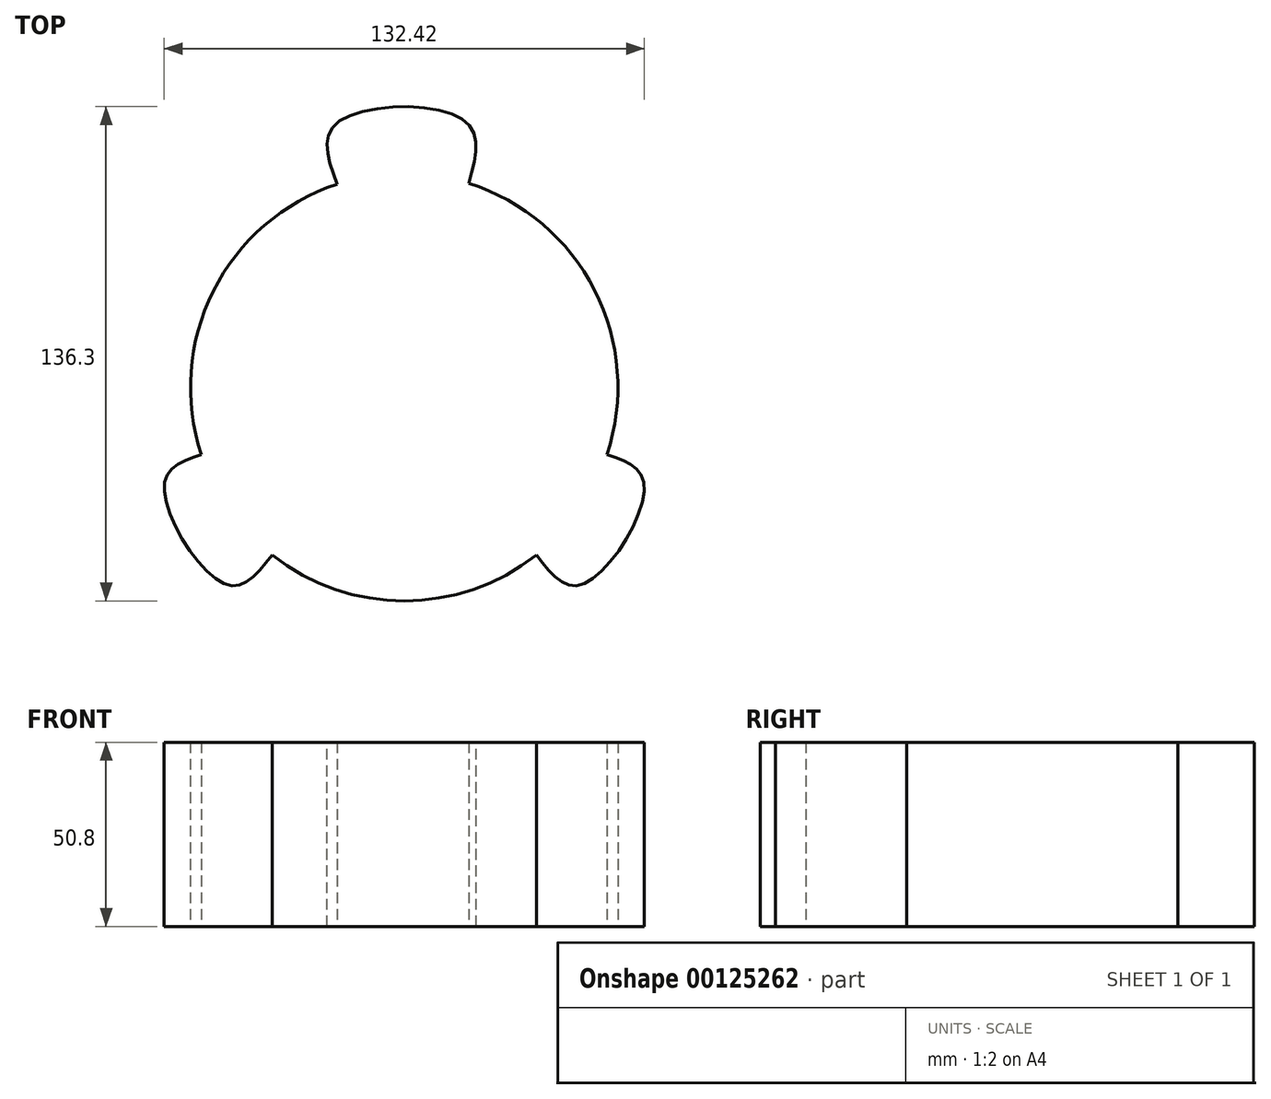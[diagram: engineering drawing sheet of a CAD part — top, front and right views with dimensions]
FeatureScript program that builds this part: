
annotation { "Feature Type Name" : "Feature", "Feature Type Description" : "" }
export const myFeature = defineFeature(function(context is Context, id is Id, definition is map)
    precondition{}
    {
        {
            var Q0;
            Q0=qCreatedBy(makeId("Top.planeOp"),FACE);
            var sketch = newSketch(context, id + "F0", { "sketchPlane" : qUnion([Q0])});
            skArc(sketch, "E0", {"start": v(-36.45, -46.33) * mm, "mid": v(0, -58.95) * mm, "end": v(36.45, -46.33) * mm});
            skFitSpline(sketch, "E1", {"points": [v(-18.53, 55.96) * mm, v(-18.61, 72.77) * mm, v(16.54, 73.55) * mm, v(17.83, 56.2) * mm], "startDerivative": vector(-24.54, 67) * mm, "endDerivative": vector(-19.45, -69.27) * mm});
            skFitSpline(sketch, "E2", {"points": [v(-55.94, -18.61) * mm, v(-66.18, -27.01) * mm, v(-49.12, -54.42) * mm, v(-36.45, -46.33) * mm], "startDerivative": vector(-53.59, -17.53) * mm, "endDerivative": vector(38.75, 50.3) * mm});
            skFitSpline(sketch, "E3.MirrorCS", {"points": [v(55.94, -18.61) * mm, v(66.18, -27.01) * mm, v(49.12, -54.42) * mm, v(36.45, -46.33) * mm], "startDerivative": vector(53.59, -17.53) * mm, "endDerivative": vector(-38.75, 50.3) * mm});
            skArc(sketch, "E4.trimOffspring", {"start": v(55.94, -18.61) * mm, "mid": v(52.53, 26.76) * mm, "end": v(17.83, 56.2) * mm});
            skArc(sketch, "E5.trimOffspring", {"start": v(-18.53, 55.96) * mm, "mid": v(-52.7, 26.43) * mm, "end": v(-55.94, -18.61) * mm});
            skSolve(sketch);
        }
        {
            var Q0;
            Q0 = qSketchRegion(id + "F0", true);
            extrude(context, id + "F1", {"entities" : qUnion([Q0]), "depth" : 50.8 * mm});
        }
    });
